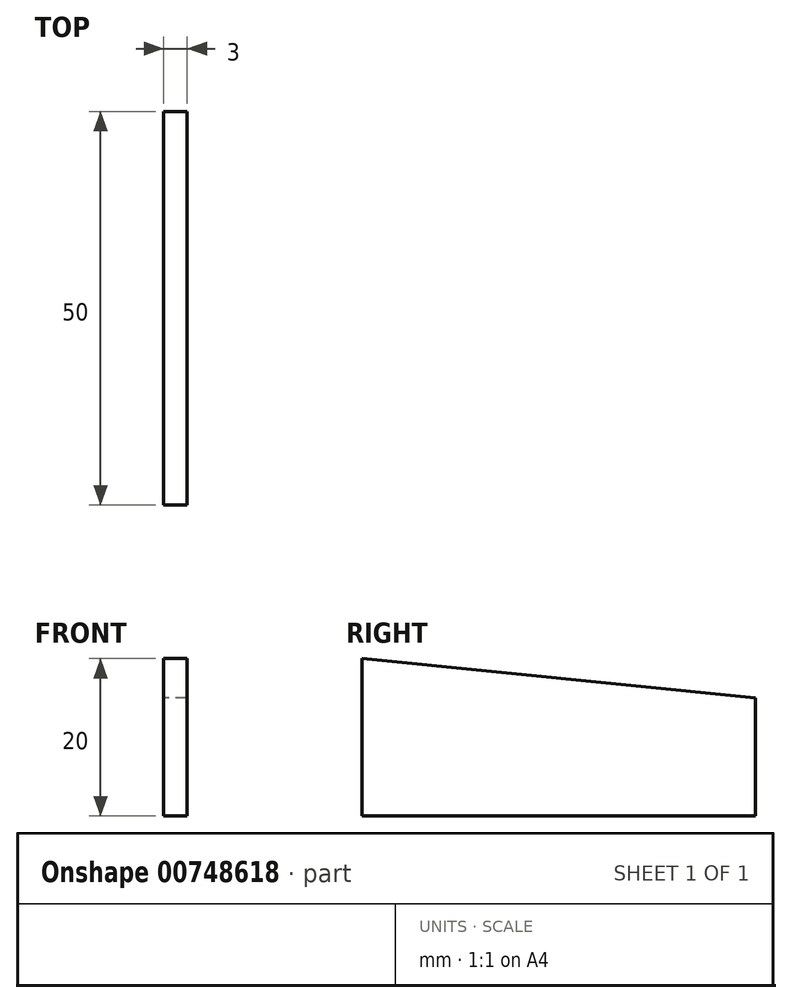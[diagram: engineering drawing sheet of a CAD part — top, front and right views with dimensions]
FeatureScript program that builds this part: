
annotation { "Feature Type Name" : "Feature", "Feature Type Description" : "" }
export const myFeature = defineFeature(function(context is Context, id is Id, definition is map)
    precondition{}
    {
        {
            var Q0;
            Q0=qCreatedBy(makeId("Right.planeOp"),FACE);
            var sketch = newSketch(context, id + "F0", { "sketchPlane" : qUnion([Q0])});
            skLineSegment(sketch, "E0", {"start": v(0, 0) * mm, "end": v(-50, 0) * mm});
            skLineSegment(sketch, "E1", {"start": v(-50, 0) * mm, "end": v(-50, 20) * mm});
            skLineSegment(sketch, "E2", {"start": v(-50, 20) * mm, "end": v(0, 15) * mm});
            skLineSegment(sketch, "E3", {"start": v(0, 15) * mm, "end": v(0, 0) * mm});
            skSolve(sketch);
        }
        {
            var Q0;
            Q0=makeQuery(id+"F0.imprint","IMPRINT",FACE,{"disambiguationData":[TD([[makeQuery(id+"F0.imprint","IMPRINT",EDGE,{"derivedFrom":sQuery(id+"F0.wireOp",EDGE,"E0")}),-1.0]])]});
            extrude(context, id + "F1", {"entities" : qUnion([Q0]), "depth" : 3 * mm, "offsetDistance" : 25 * mm});
        }
    });
